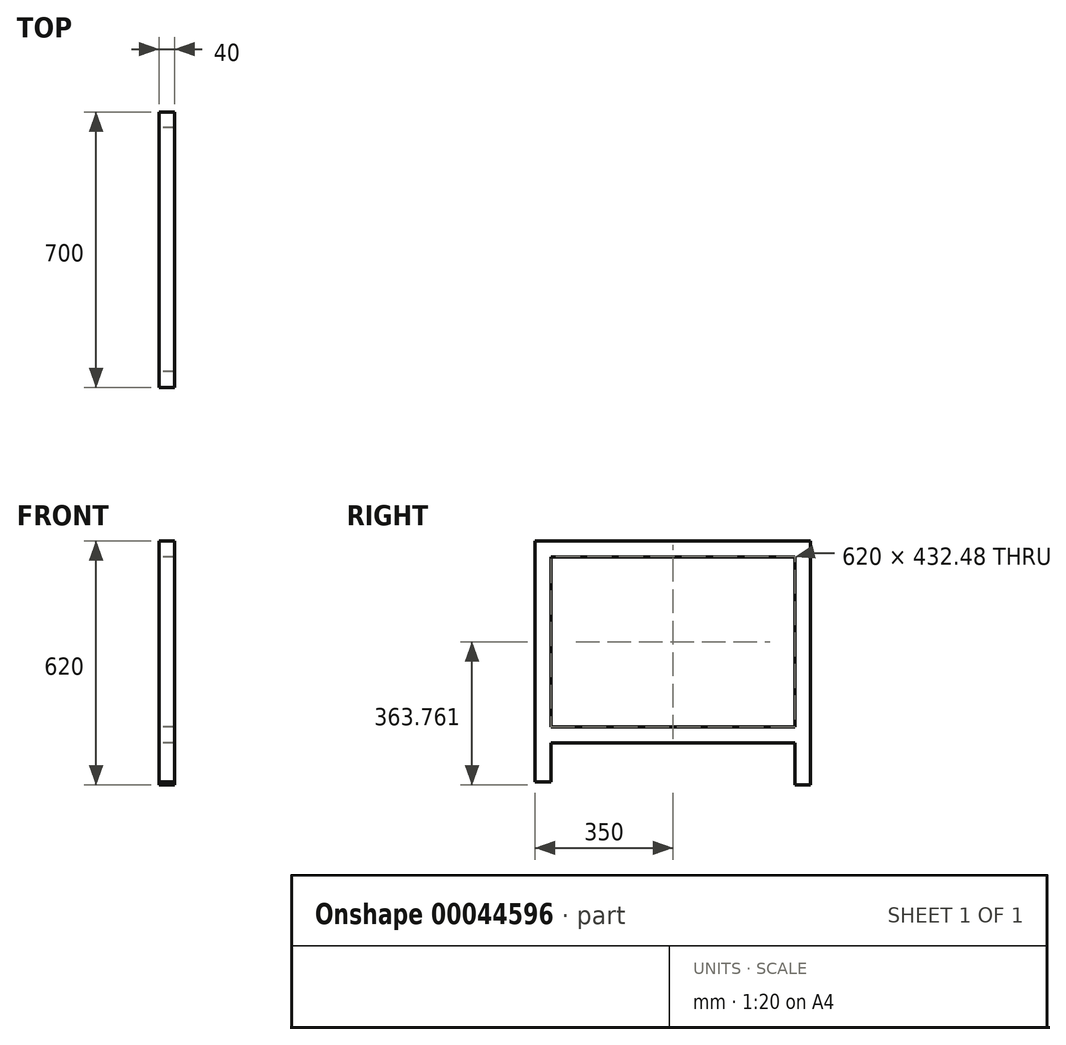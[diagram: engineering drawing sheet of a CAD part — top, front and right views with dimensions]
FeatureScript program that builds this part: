
annotation { "Feature Type Name" : "Feature", "Feature Type Description" : "" }
export const myFeature = defineFeature(function(context is Context, id is Id, definition is map)
    precondition{}
    {
        {
            var Q0;
            Q0=qCreatedBy(makeId("Right.planeOp"),FACE);
            var sketch = newSketch(context, id + "F0", { "sketchPlane" : qUnion([Q0])});
            skLineSegment(sketch, "E0", {"start": v(406.86, 0) * mm, "end": v(-293.14, 0) * mm});
            skLineSegment(sketch, "E1", {"start": v(-293.14, 0) * mm, "end": v(-293.14, -612.48) * mm});
            skLineSegment(sketch, "E2", {"start": v(-293.14, -612.48) * mm, "end": v(-253.14, -612.48) * mm});
            skLineSegment(sketch, "E3", {"start": v(-253.14, -472.48) * mm, "end": v(-253.14, -40) * mm});
            skLineSegment(sketch, "E4", {"start": v(-253.14, -40) * mm, "end": v(366.86, -40) * mm});
            skLineSegment(sketch, "E5", {"start": v(366.86, -40) * mm, "end": v(366.86, -472.48) * mm});
            skLineSegment(sketch, "E6", {"start": v(366.86, -620) * mm, "end": v(406.86, -620) * mm});
            skLineSegment(sketch, "E7", {"start": v(406.86, -620) * mm, "end": v(406.86, 0) * mm});
            skLineSegment(sketch, "E8", {"start": v(-253.14, -472.48) * mm, "end": v(366.86, -472.48) * mm});
            skLineSegment(sketch, "E9", {"start": v(-253.14, -512.48) * mm, "end": v(366.86, -512.48) * mm});
            skLineSegment(sketch, "E10.trimOffspring", {"start": v(366.86, -512.48) * mm, "end": v(366.86, -620) * mm});
            skLineSegment(sketch, "E11", {"start": v(-253.14, -512.48) * mm, "end": v(-253.14, -612.48) * mm});
            skSolve(sketch);
        }
        {
            var Q0;
            Q0=makeQuery(id+"F0.imprint","IMPRINT",FACE,{"disambiguationData":[TD([[makeQuery(id+"F0.imprint","IMPRINT",EDGE,{"derivedFrom":sQuery(id+"F0.wireOp",EDGE,"E0")}),1.0]])]});
            var Q1;
            {var subQ4=sQuery(id+"F0.wireOp",EDGE,"4af0bac2-3396-4662-9392-efa54b85aefb");Q1=makeQuery(id+"F0.imprint","IMPRINT",FACE,{"disambiguationData":[TD([[makeQuery(id+"F0.imprint","IMPRINT",EDGE,{"derivedFrom":subQ4}),-1.0]])]});}
            var Q2;
            {var subQ1=sQuery(id+"F0.wireOp",EDGE,"e2bfed3c-d66f-4b53-bfc3-2d2430176155");Q2=makeQuery(id+"F0.imprint","IMPRINT",FACE,{"disambiguationData":[TD([[makeQuery(id+"F0.imprint","IMPRINT",EDGE,{"derivedFrom":subQ1}),1.0]])]});}
            extrude(context, id + "F1", {"entities" : qUnion([Q0, Q1, Q2]), "depth" : 40 * mm});
        }
    });
